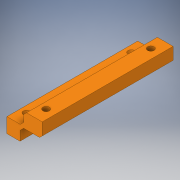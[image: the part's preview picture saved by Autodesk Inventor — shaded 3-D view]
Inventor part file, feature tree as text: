
AUTODESK INVENTOR PART (.ipt)
format: ipt  version: 2019 (Build 230136000, 136)  size: 144,384 bytes
history: native  units: in
note: dims shown in document units (in); Inventor stores cm internally (conversion verified against a paired STEP export)
features: sketch x3, hole x2, chamfer x2, extrude x1
ambient origin geometry x8: Origin, YZ Plane, XZ Plane, XY Plane, X Axis, Y Axis, Z Axis, Center Point
bodies: Solid1 (feature_tree)
feature tree (8):
  extrude  "Extrusion1"  Depth=0.65in
  hole  "Hole2"  [1 undecoded]
  hole  "Hole3"  [1 undecoded]
  chamfer  "Chamfer1"  Distance=0.5in
  chamfer  "Chamfer2"  Distance=0.25in
  sketch  "Sketch1"  dims[d0=0.565in d2=0.65in]
  sketch  "Sketch3"  dims[d6=0.7in d9=0.85in]
  sketch  "Sketch4"  dims[d10=5.0in d11=0.0in d25=0.5in d26=0.5in d27=0.25in d28=0.25in d29=0.25in d30=0.75in d31=0.375in d32=0.25in d33=0.5635in d34=1.0in d35=0.8108in d36=0.35in d37=0.5in d38=0.5in d39=0.25in d40=0.75in d41=0.375in d42=0.25in d43=0.5635in d44=1.0in d45=0.8108in d47=0.565in d48=0.7in d49=0.5in d62=0.14in d63=0.125in d64=45.0deg d71=0.1in d72=0.125in d73=45.0deg d18=1.0in d19=1.0in d20=1.0in d21=0.15in d22=0.25in d23=0.375in d24=0.5635in]
note: 2 required parameter values undecoded (feature->parameter linkage not recoverable at this tier; creation-order binding heuristic only, values carry confidence <= 0.55)
